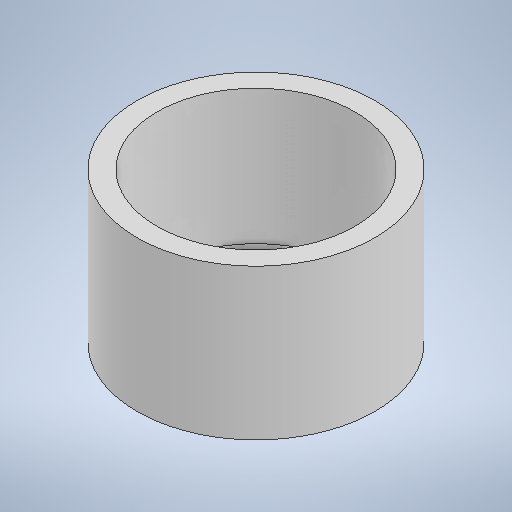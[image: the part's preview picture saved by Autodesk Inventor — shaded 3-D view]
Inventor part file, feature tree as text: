
AUTODESK INVENTOR PART (.ipt)
format: ipt  version: 2025 (Build 290162000, 162)  size: 204,288 bytes
history: native  units: in
note: dims shown in document units (in); Inventor stores cm internally (conversion verified against a paired STEP export)
features: sketch x4, extrude x2
ambient origin geometry x8: Origin, YZ Plane, XZ Plane, XY Plane, X Axis, Y Axis, Z Axis, Center Point
bodies: Solid1 (feature_tree)
feature tree (6):
  sketch  "Sketch1"  dims[d0=23.622in d1=14.9606in d2=0.0in]
  sketch  "Sketch2"  dims[d3=19.685in d4=13.3858in d5=0.0in]
  sketch  "Sketch3"
  extrude  "Extrusion1"  Depth=14.9606in TaperAngle=0.0deg
  extrude  "Extrusion2"  Depth=13.3858in TaperAngle=0.0deg
  sketch  "Sketch4"
